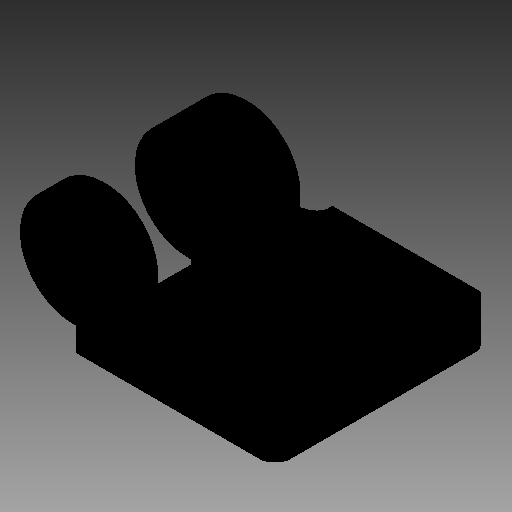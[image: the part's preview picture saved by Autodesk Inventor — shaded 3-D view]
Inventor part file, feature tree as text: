
AUTODESK INVENTOR PART (.ipt)
format: ipt  version: 2019 (Build 230136000, 136)  size: 211,456 bytes
history: native  units: in
note: dims shown in document units (in); Inventor stores cm internally (conversion verified against a paired STEP export)
features: sketch x9, extrude x7, other x7, revolve x2
ambient origin geometry x8: Origin, YZ Plane, XZ Plane, XY Plane, X Axis, Y Axis, Z Axis, Center Point
bodies: Solid1 (feature_tree)
feature tree (25):
  extrude  "Extrusion1"  Depth=1.5748in TaperAngle=0.0deg
  extrude  "Extrusion2"  Depth=1.5748in TaperAngle=0.0deg
  extrude  "Extrusion3"  TaperAngle=360.0deg  [1 undecoded]
  extrude  "Extrusion4"  TaperAngle=360.0deg  [1 undecoded]
  extrude  "Extrusion5"  [1 undecoded]
  revolve  "Revolution1"  [1 undecoded]
  extrude  "Extrusion6"  [1 undecoded]
  revolve  "Revolution2"  [1 undecoded]
  extrude  "Extrusion7"  [1 undecoded]
  other  "to_a_XY"
  other  "to_a_YZ"
  other  "to_a_ZX"
  other  "to_a_X"
  other  "to_a_Y"
  other  "to_a_Z"
  other  "to_a_Center"
  sketch  "Sketch_1"  dims[d0=0.312in d1=0.0in d2=1.5748in d3=0.0in]
  sketch  "Sketch_2"  dims[d4=2.9134in d5=0.0in d6=1.5748in d7=0.0in]
  sketch  "Sketch_3"  dims[d8=0.462in d9=0.0in d10=360.0deg]
  sketch  "Sketch_4"  dims[d11=0.462in d12=0.0in d13=360.0deg]
  sketch  "Sketch_5"  dims[d14=1.5748in d15=0.0in]
  sketch  "Sketch_6"
  sketch  "Sketch_7"
  sketch  "Sketch_8"
  sketch  "Sketch_9"
note: 7 required parameter values undecoded (feature->parameter linkage not recoverable at this tier; creation-order binding heuristic only, values carry confidence <= 0.55)
